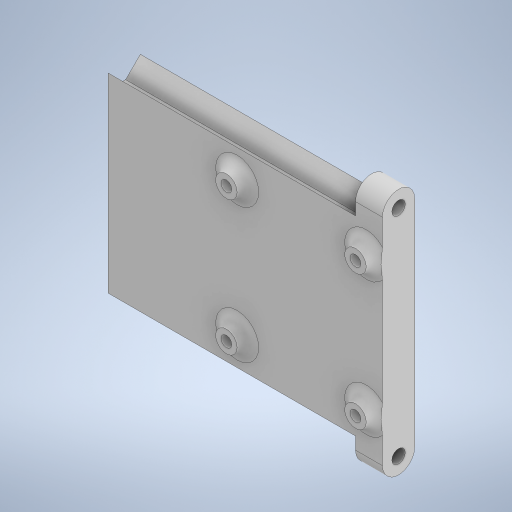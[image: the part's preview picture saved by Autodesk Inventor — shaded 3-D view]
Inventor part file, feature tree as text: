
AUTODESK INVENTOR PART (.ipt)
format: ipt  version: 2023 (Build 270158000, 158)  size: 339,456 bytes
history: native  units: mm
features: extrude x4, sketch x4, projected_geometry x2, other x1, fillet x1
ambient origin geometry x8: Origin, YZ Plane, XZ Plane, XY Plane, X Axis, Y Axis, Z Axis, Center Point
bodies: Body1 (feature_tree)
feature tree (12):
  other  "솔리드1"
  extrude  "돌출1"  Depth=51.0mm
  extrude  "돌출3"  Depth=30.0mm
  extrude  "돌출5"  Depth=2.0mm
  extrude  "돌출6"  Depth=15.0mm
  fillet  "모깎기1"  Radius=25.0mm
  sketch  "스케치1"
  sketch  "스케치4"
  projected_geometry  "투영된 루프1"
  sketch  "스케치6"
  projected_geometry  "투영된 루프2"
  sketch  "스케치7"
